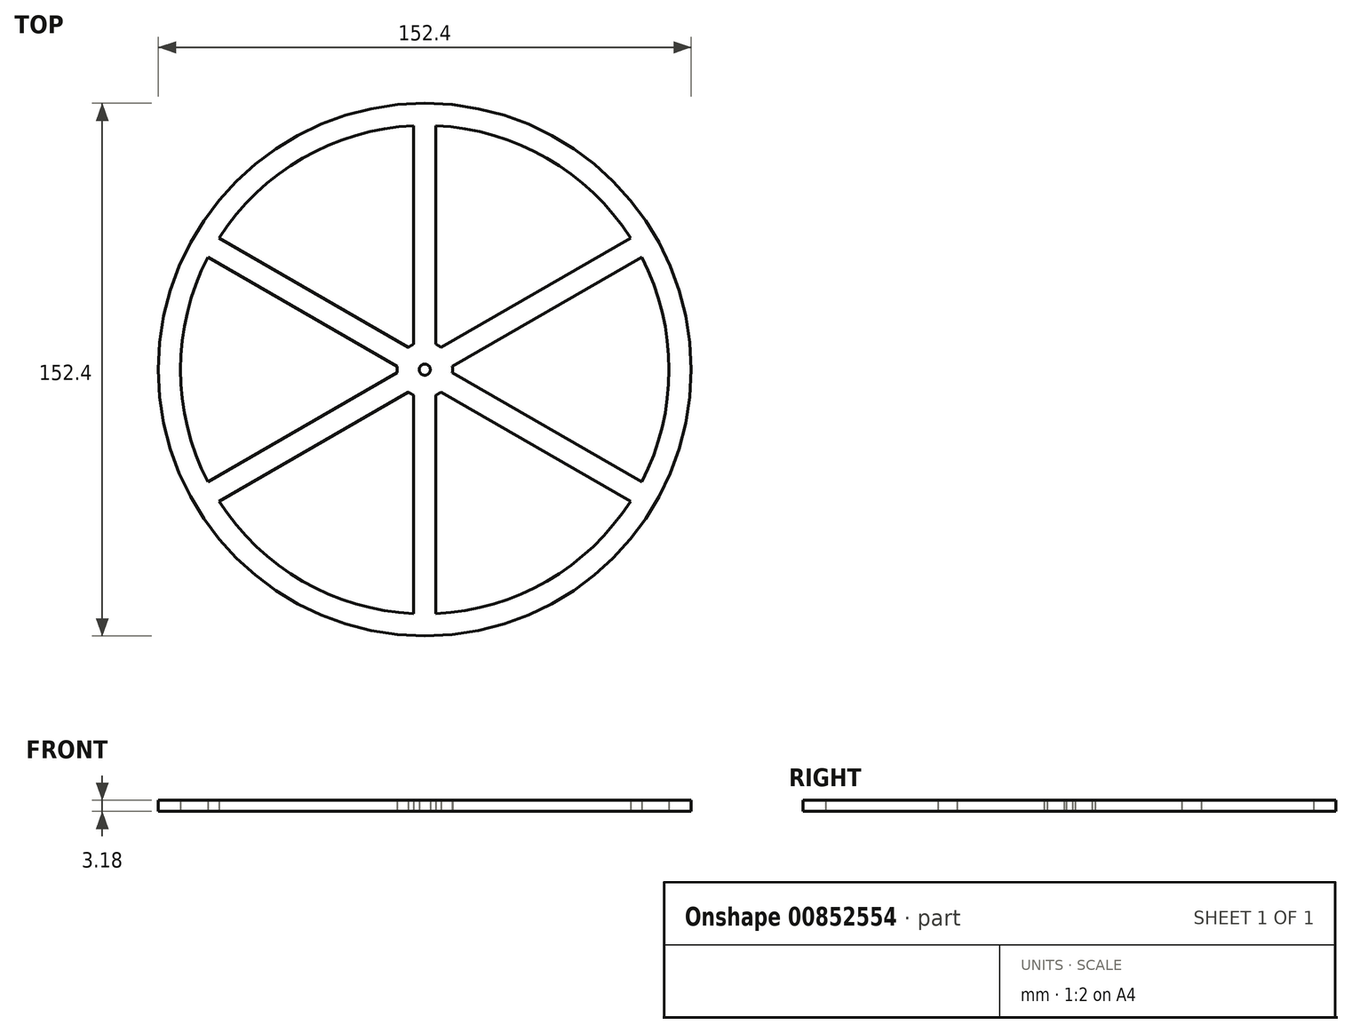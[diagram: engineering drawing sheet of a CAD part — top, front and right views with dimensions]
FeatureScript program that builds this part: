
annotation { "Feature Type Name" : "Feature", "Feature Type Description" : "" }
export const myFeature = defineFeature(function(context is Context, id is Id, definition is map)
    precondition{}
    {
        {
            var Q0;
            Q0=qCreatedBy(makeId("Top.planeOp"),FACE);
            var sketch = newSketch(context, id + "F0", { "sketchPlane" : qUnion([Q0])});
            skCircle(sketch, "E0", {"center": v(0, 0) * mm, "radius": 76.2 * mm});
            skCircle(sketch, "E1", {"center": v(0, 0) * mm, "radius": 1.59 * mm});
            skCircle(sketch, "E2", {"center": v(0, 0) * mm, "radius": 69.85 * mm});
            skCircle(sketch, "E3", {"center": v(0, 0) * mm, "radius": 7.94 * mm});
            skLineSegment(sketch, "E4", {"start": v(-3.17, 7.27) * mm, "end": v(-3.18, 69.78) * mm});
            skLineSegment(sketch, "E5", {"start": v(3.18, 7.27) * mm, "end": v(3.17, 69.78) * mm});
            skLineSegment(sketch, "E6.1.0", {"start": v(-7.89, 0.89) * mm, "end": v(-62.02, 32.14) * mm});
            skLineSegment(sketch, "E6.1.1", {"start": v(-4.71, 6.39) * mm, "end": v(-58.84, 37.64) * mm});
            skLineSegment(sketch, "E6.2.0", {"start": v(-4.71, -6.39) * mm, "end": v(-58.84, -37.64) * mm});
            skLineSegment(sketch, "E6.2.1", {"start": v(-7.89, -0.89) * mm, "end": v(-62.02, -32.14) * mm});
            skLineSegment(sketch, "E6.3.0", {"start": v(3.17, -7.27) * mm, "end": v(3.17, -69.78) * mm});
            skLineSegment(sketch, "E6.3.1", {"start": v(-3.18, -7.27) * mm, "end": v(-3.18, -69.78) * mm});
            skLineSegment(sketch, "E6.4.0", {"start": v(7.89, -0.89) * mm, "end": v(62.02, -32.14) * mm});
            skLineSegment(sketch, "E6.4.1", {"start": v(4.71, -6.39) * mm, "end": v(58.84, -37.64) * mm});
            skLineSegment(sketch, "E6.5.0", {"start": v(4.71, 6.39) * mm, "end": v(58.84, 37.64) * mm});
            skLineSegment(sketch, "E6.5.1", {"start": v(7.89, 0.89) * mm, "end": v(62.02, 32.14) * mm});
            skLineSegment(sketch, "E7", {"start": v(-3.17, 7.27) * mm, "end": v(3.18, 7.27) * mm});
            skSolve(sketch);
        }
        {
            var Q0;
            Q0=qSketchRegion(id+"F0",true);
            var Q1;
            Q1=makeQuery(id+"F0.imprint","IMPRINT",FACE,{"disambiguationData":[TD([[makeQuery(id+"F0.imprint","IMPRINT",EDGE,{"derivedFrom":sQuery(id+"F0.wireOp",EDGE,"E0")}),1.0]])]});
            var Q2;
            {var subQ0=sQuery(id+"F0.wireOp",EDGE,"E6.1.0");Q2=makeQuery(id+"F0.imprint","IMPRINT",FACE,{"disambiguationData":[TD([[makeQuery(id+"F0.imprint","IMPRINT",EDGE,{"derivedFrom":subQ0}),-1.0]])]});}
            var Q3;
            {var subQ0=sQuery(id+"F0.wireOp",EDGE,"E6.2.0");Q3=makeQuery(id+"F0.imprint","IMPRINT",FACE,{"disambiguationData":[TD([[makeQuery(id+"F0.imprint","IMPRINT",EDGE,{"derivedFrom":subQ0}),-1.0]])]});}
            var Q4;
            Q4=makeQuery(id+"F0.imprint","IMPRINT",FACE,{"disambiguationData":[TD([[makeQuery(id+"F0.imprint","IMPRINT",EDGE,{"derivedFrom":sQuery(id+"F0.wireOp",EDGE,"E1")}),-1.0]])]});
            var Q5;
            {var subQ0=sQuery(id+"F0.wireOp",EDGE,"E6.3.0");Q5=makeQuery(id+"F0.imprint","IMPRINT",FACE,{"disambiguationData":[TD([[makeQuery(id+"F0.imprint","IMPRINT",EDGE,{"derivedFrom":subQ0}),-1.0]])]});}
            var Q6;
            {var subQ0=sQuery(id+"F0.wireOp",EDGE,"E6.4.0");Q6=makeQuery(id+"F0.imprint","IMPRINT",FACE,{"disambiguationData":[TD([[makeQuery(id+"F0.imprint","IMPRINT",EDGE,{"derivedFrom":subQ0}),-1.0]])]});}
            var Q7;
            {var subQ0=sQuery(id+"F0.wireOp",EDGE,"E6.5.0");Q7=makeQuery(id+"F0.imprint","IMPRINT",FACE,{"disambiguationData":[TD([[makeQuery(id+"F0.imprint","IMPRINT",EDGE,{"derivedFrom":subQ0}),-1.0]])]});}
            var Q8;
            {var subQ0=sQuery(id+"F0.wireOp",EDGE,"E4");Q8=makeQuery(id+"F0.imprint","IMPRINT",FACE,{"disambiguationData":[TD([[makeQuery(id+"F0.imprint","IMPRINT",EDGE,{"derivedFrom":subQ0}),-1.0]])]});}
            var Q9;
            {var subQ0=sQuery(id+"F0.wireOp",EDGE,"E7");Q9=makeQuery(id+"F0.imprint","IMPRINT",FACE,{"disambiguationData":[TD([[makeQuery(id+"F0.imprint","IMPRINT",EDGE,{"derivedFrom":subQ0}),1.0]])]});}
            extrude(context, id + "F1", {"entities" : qUnion([Q0, Q1, Q2, Q3, Q4, Q5, Q6, Q7, Q8, Q9]), "depth" : 3.17 * mm, "offsetDistance" : 25.4 * mm});
        }
    });
